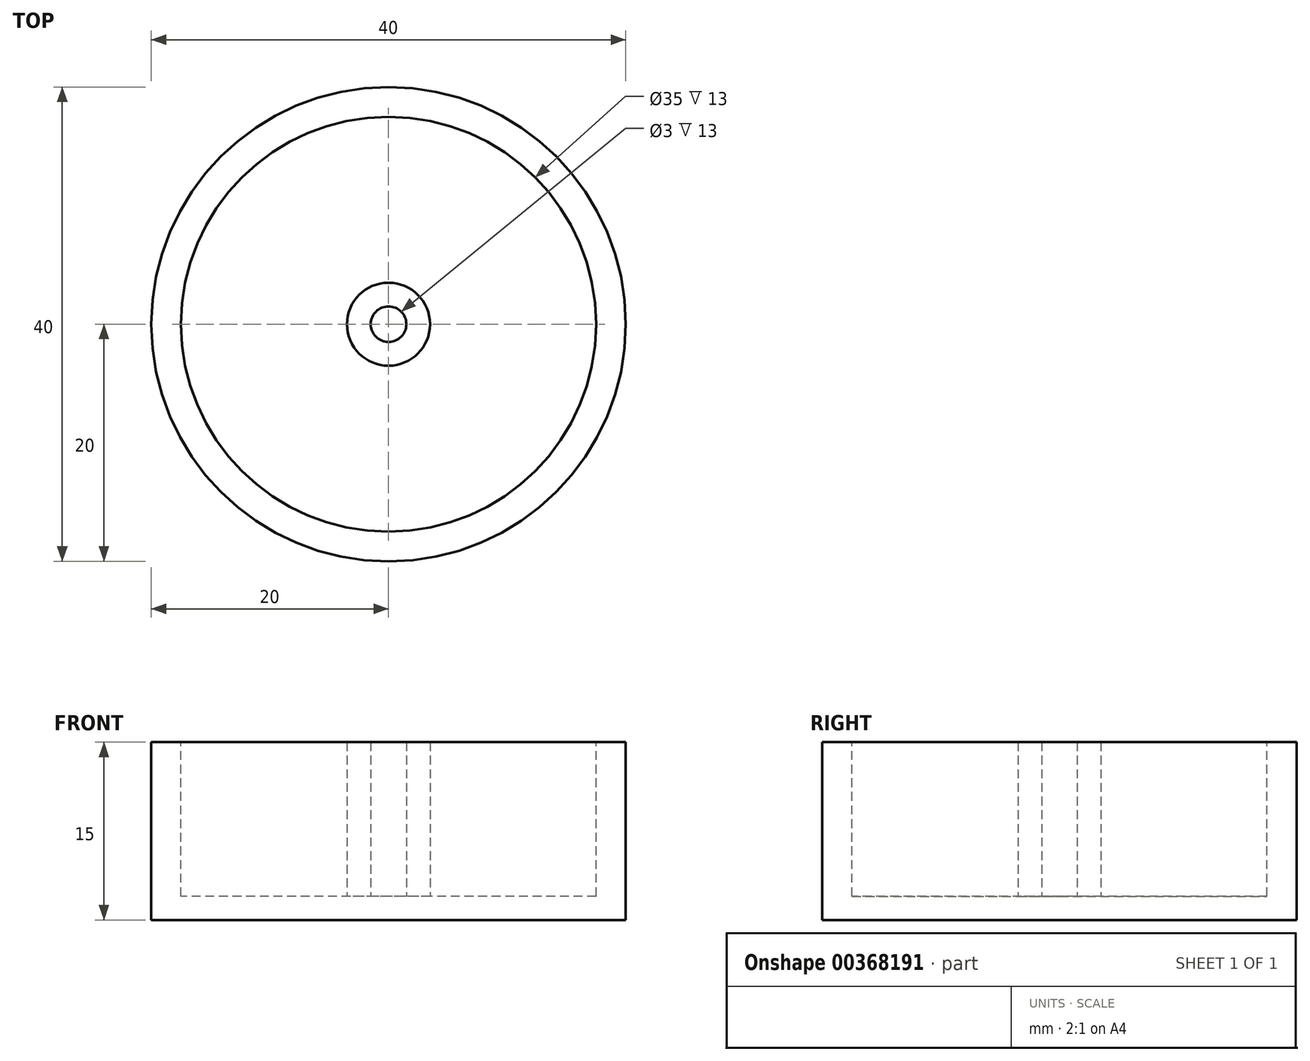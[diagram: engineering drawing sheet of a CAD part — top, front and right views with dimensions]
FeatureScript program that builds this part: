
annotation { "Feature Type Name" : "Feature", "Feature Type Description" : "" }
export const myFeature = defineFeature(function(context is Context, id is Id, definition is map)
    precondition{}
    {
        {
            var Q0;
            Q0=qCreatedBy(makeId("Top.planeOp"),FACE);
            var sketch = newSketch(context, id + "F0", { "sketchPlane" : qUnion([Q0])});
            skCircle(sketch, "E0", {"center": v(0, 0) * mm, "radius": 20 * mm});
            skSolve(sketch);
        }
        {
            var Q0;
            Q0 = qSketchRegion(id + "F0", true);
            extrude(context, id + "F1", {"entities" : qUnion([Q0]), "depth" : 15 * mm});
        }
        {
            var Q0;
            Q0=makeQuery(id+"F1.opExtrude","CAP_FACE",FACE,{"disambiguationData":[OSD([sQuery(id+"F0.wireOp",EDGE,"E0")])],"isStart":false});
            var sketch = newSketch(context, id + "F2", { "sketchPlane" : qUnion([Q0])});
            skCircle(sketch, "E1", {"center": v(0, 0) * mm, "radius": 17.5 * mm});
            skSolve(sketch);
        }
        {
            var Q0;
            Q0 = qSketchRegion(id + "F2", true);
            extrude(context, id + "F3", {"entities" : qUnion([Q0]), "operationType" : NewBodyOperationType.REMOVE, "oppositeDirection" : true, "depth" : 13 * mm});
        }
        {
            var Q0;
            Q0=makeQuery(id+"F3.boolean.opBoolean","COPY",FACE,{"derivedFrom":makeQuery(id+"F3.opExtrude","CAP_FACE",FACE,{"disambiguationData":[OSD([sQuery(id+"F2.wireOp",EDGE,"E1")])],"isStart":false})});
            var sketch = newSketch(context, id + "F4", { "sketchPlane" : qUnion([Q0])});
            skCircle(sketch, "E2", {"center": v(0, 0) * mm, "radius": 3.5 * mm});
            skCircle(sketch, "E3", {"center": v(0, 0) * mm, "radius": 1.5 * mm});
            skSolve(sketch);
        }
        {
            var Q0;
            Q0 = qSketchRegion(id + "F4", true);
            extrude(context, id + "F5", {"entities" : qUnion([Q0]), "operationType" : NewBodyOperationType.ADD, "depth" : 13 * mm});
        }
    });
